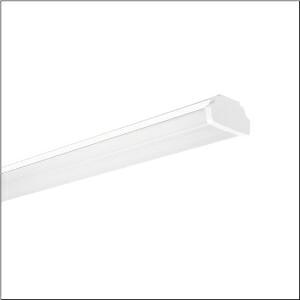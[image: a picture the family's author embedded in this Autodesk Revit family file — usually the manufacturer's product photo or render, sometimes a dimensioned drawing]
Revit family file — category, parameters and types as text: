
# Revit family: modario_r__31_mo_53bm812c1v6075_d0f6
name_source: partatom
category: Lighting Fixtures
units: mm (PartAtom-declared; Revit-internal decimal feet)

## family parameters
Cut with Voids When Loaded = No
Host = Face
Light Source = No
Part Type = Normal
Room Calculation Point = No
Round Connector Dimension = Use Diameter
Shared = No

## types (1)
- --- (1 x LED, 7640 lm, 48.9 W, 6500K)
    Apparent Load = 49 VA
    CIE Flux Codes = 47 80 95 92 100
    Color Rendering = 80
    Color Temperature = 6500K
    Default Elevation = 1800 mm
    Description = Modario® 31 MO, luminaire insert, of sheet steel, coil coated, white, length: 1.495mm, width: 81mm, height: 82mm, 5x system unit, system units: 299mm, LED rated luminous flux: 7.640lm, light colour: 865, control gear: ON/OFF Multilumen, CLOi, control gear: ECG Multilumen, with plug, 3-pole, with phase selection, mains connection: 220..240V, AC, 50/60Hz, start of lifetime: 49W, end of service life: 56W, through-wiring accessed according to module size, primary optical cover: cover, of PMMA, light emission: direct distribution, primary light characteristic: symmetric, protection rating (complete): IP20, protection rating (LED compartment): IP50, insulation class (complete): insulation class I (protective earthing), certification: CE, ENEC, VDE, UKCA, impact resistance: IK03, permissible ambient temperature for indoor applications: -35..+30°C, corresponds to IFS (International Featured Standards) requirements for safety and quality in the food industry, reducing of maximum allowable ambient temperature of 5°C with ceiling mounting, packaging unit: 1 piece
    Height = 92 mm
    Lamp = 1 x LED
    Lamp Light Flux = 7640 lm
    Lamp Power = 48.9 W
    Lamp count = 1
    Length = 1495 mm
    Luminous efficacy = 156 lm/W
    Manufacturer = Siteco
    ModVariant = No
    Model = 53BM812C1V6075
    Mounting Place = Ceiling
    Mounting Type = Pendant
    Number of Poles = 1
    OnlyDefault = Yes
    Power Factor = 1
    Product Name = Modario® 31 MO
    Product group = luminaire insert
    ProductGroupID = 901
    Protection Class = Protection class I
    Protection Degree = IP 20
    RLX_Detail_Level = 1
    RLX_Emergency_Light_Flux = 0 lm
    RLX_Emergency_Type = 0
    RLX_Emergency_Type_DB = No
    RlxData = <blob elided: 40037 chars, md5=1655dc62>
    Socket = socket
    Standby Power = 0 W
    System Light Flux = 7640 lm
    System Power = 49 W
    Type Comments = factory setting: luminous flux: 100 % | (A | C | E) | 107 mA
    Type Image = l_1300283.jpg
    URL = http://relux.com
    VarID = @adj_138175
    Voltage = 0 V
    Weight = 0.00 kg
    Width = 81 mm

## geometry (parser evidence)
native form markers: Blend x4, Sweep x13
no freeform markers — native parametric forms only
